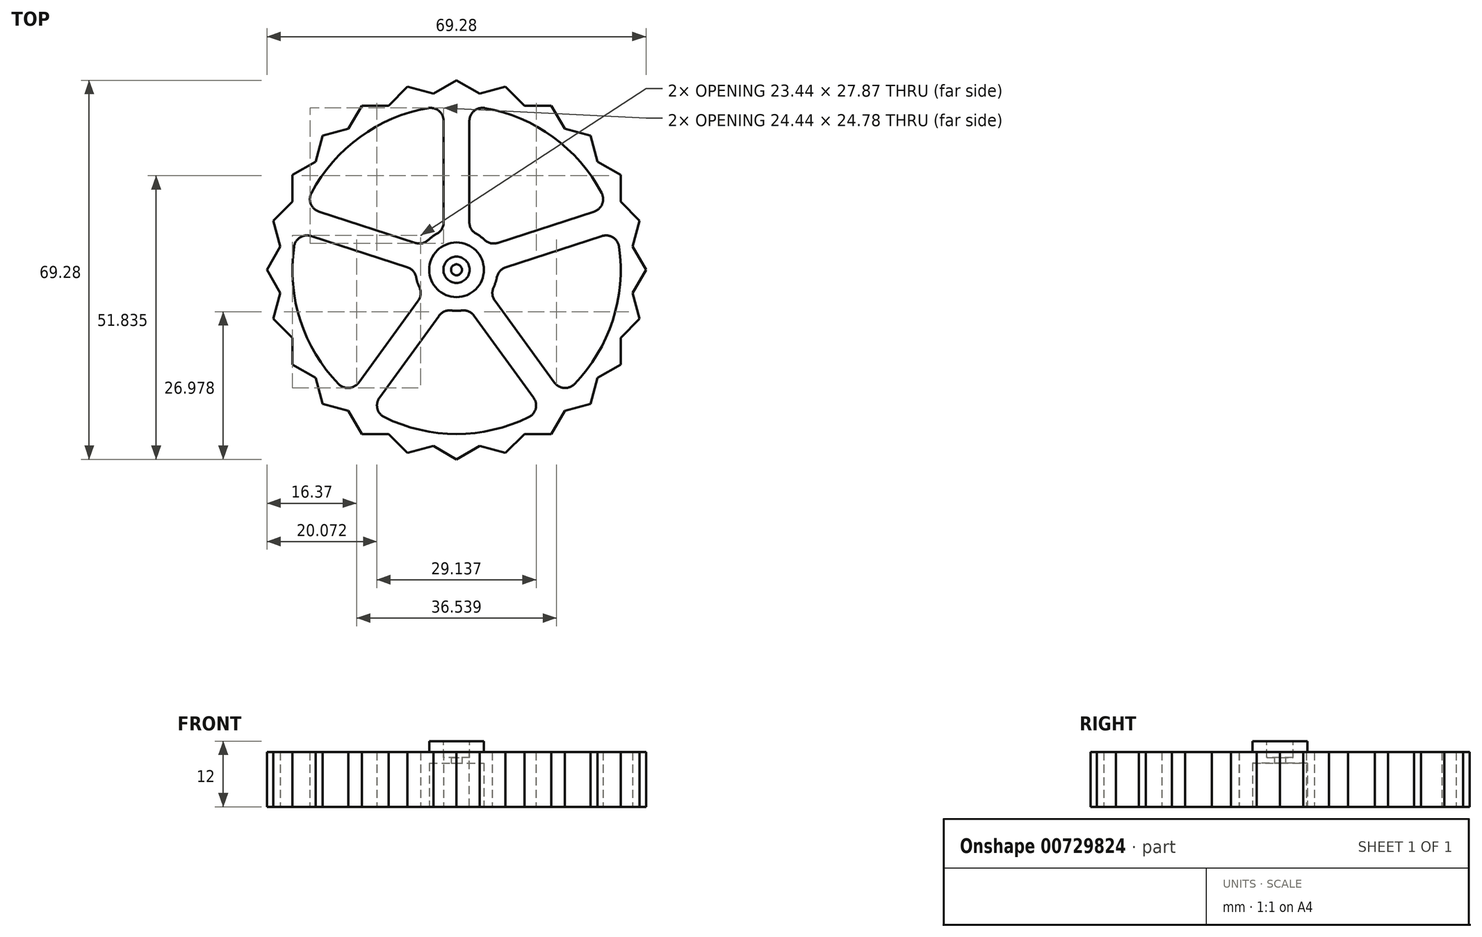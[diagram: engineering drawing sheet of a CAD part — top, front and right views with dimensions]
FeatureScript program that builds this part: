
annotation { "Feature Type Name" : "Feature", "Feature Type Description" : "" }
export const myFeature = defineFeature(function(context is Context, id is Id, definition is map)
    precondition{}
    {
        {
            var Q0;
            Q0=qCreatedBy(makeId("Top.planeOp"),FACE);
            var sketch = newSketch(context, id + "F0", { "sketchPlane" : qUnion([Q0])});
            skCircle(sketch, "E0", {"center": v(0, 0) * mm, "radius": 30 * mm});
            skCircle(sketch, "E1", {"center": v(0, 0) * mm, "radius": 2.35 * mm});
            skCircle(sketch, "E2.cCircle", {"center": v(0, 0) * mm, "radius": 30 * mm, "construction": true});
            skLineSegment(sketch, "E2.0", {"start": v(-17.32, 30) * mm, "end": v(17.32, 30) * mm});
            skLineSegment(sketch, "E2.1", {"start": v(17.32, 30) * mm, "end": v(34.64, 0) * mm});
            skLineSegment(sketch, "E2.2", {"start": v(34.64, 0) * mm, "end": v(17.32, -30) * mm});
            skLineSegment(sketch, "E2.3", {"start": v(17.32, -30) * mm, "end": v(-17.32, -30) * mm});
            skLineSegment(sketch, "E2.4", {"start": v(-17.32, -30) * mm, "end": v(-34.64, 0) * mm});
            skLineSegment(sketch, "E2.5", {"start": v(-34.64, 0) * mm, "end": v(-17.32, 30) * mm});
            skPoint(sketch, "E2.0.midPoint", {"position": v(0, 30) * mm});
            skLineSegment(sketch, "E3", {"start": v(0, 0) * mm, "end": v(25.98, 15) * mm, "construction": true});
            skLineSegment(sketch, "E4.0", {"start": v(30, 17.32) * mm, "end": v(30, -17.32) * mm});
            skLineSegment(sketch, "E4.1", {"start": v(30, -17.32) * mm, "end": v(0, -34.64) * mm});
            skLineSegment(sketch, "E4.2", {"start": v(0, -34.64) * mm, "end": v(-30, -17.32) * mm});
            skLineSegment(sketch, "E4.3", {"start": v(-30, -17.32) * mm, "end": v(-30, 17.32) * mm});
            skLineSegment(sketch, "E4.4", {"start": v(-30, 17.32) * mm, "end": v(0, 34.64) * mm});
            skLineSegment(sketch, "E4.5", {"start": v(0, 34.64) * mm, "end": v(30, 17.32) * mm});
            skPoint(sketch, "E4.0.midPoint", {"position": v(30, 0) * mm});
            skLineSegment(sketch, "E5", {"start": v(0, 0) * mm, "end": v(21.96, 21.96) * mm, "construction": true});
            skLineSegment(sketch, "E6.0", {"start": v(8.97, 33.46) * mm, "end": v(33.46, 8.97) * mm});
            skLineSegment(sketch, "E6.1", {"start": v(33.46, 8.97) * mm, "end": v(24.5, -24.5) * mm});
            skLineSegment(sketch, "E6.2", {"start": v(24.5, -24.5) * mm, "end": v(-8.97, -33.46) * mm});
            skLineSegment(sketch, "E6.3", {"start": v(-8.97, -33.46) * mm, "end": v(-33.46, -8.97) * mm});
            skLineSegment(sketch, "E6.4", {"start": v(-33.46, -8.97) * mm, "end": v(-24.5, 24.5) * mm});
            skLineSegment(sketch, "E6.5", {"start": v(-24.5, 24.5) * mm, "end": v(8.97, 33.46) * mm});
            skPoint(sketch, "E6.0.midPoint", {"position": v(21.21, 21.21) * mm});
            skLineSegment(sketch, "E7", {"start": v(0, 0) * mm, "end": v(30, 8.04) * mm, "construction": true});
            skLineSegment(sketch, "E8.0", {"start": v(24.5, 24.5) * mm, "end": v(33.46, -8.97) * mm});
            skLineSegment(sketch, "E8.1", {"start": v(33.46, -8.97) * mm, "end": v(8.97, -33.46) * mm});
            skLineSegment(sketch, "E8.2", {"start": v(8.97, -33.46) * mm, "end": v(-24.5, -24.5) * mm});
            skLineSegment(sketch, "E8.3", {"start": v(-24.5, -24.5) * mm, "end": v(-33.46, 8.97) * mm});
            skLineSegment(sketch, "E8.4", {"start": v(-33.46, 8.97) * mm, "end": v(-8.97, 33.46) * mm});
            skLineSegment(sketch, "E8.5", {"start": v(-8.97, 33.46) * mm, "end": v(24.5, 24.5) * mm});
            skPoint(sketch, "E8.0.midPoint", {"position": v(28.98, 7.76) * mm});
            skLineSegment(sketch, "E9", {"start": v(-25, 0) * mm, "end": v(22.68, 0) * mm, "construction": true});
            skLineSegment(sketch, "E10", {"start": v(-2.35, 0) * mm, "end": v(-2.35, 29.9) * mm});
            skLineSegment(sketch, "E11", {"start": v(2.35, 0) * mm, "end": v(2.35, 29.9) * mm});
            skLineSegment(sketch, "E12.1.0", {"start": v(0.73, 2.23) * mm, "end": v(-27.72, 11.48) * mm});
            skLineSegment(sketch, "E12.1.1", {"start": v(-0.73, -2.23) * mm, "end": v(-29.17, 7) * mm});
            skLineSegment(sketch, "E12.2.0", {"start": v(-1.9, 1.38) * mm, "end": v(-19.48, -22.81) * mm});
            skLineSegment(sketch, "E12.2.1", {"start": v(1.9, -1.38) * mm, "end": v(-15.68, -25.58) * mm});
            skLineSegment(sketch, "E12.3.0", {"start": v(-1.9, -1.38) * mm, "end": v(15.68, -25.58) * mm});
            skLineSegment(sketch, "E12.3.1", {"start": v(1.9, 1.38) * mm, "end": v(19.48, -22.81) * mm});
            skLineSegment(sketch, "E12.4.0", {"start": v(0.73, -2.23) * mm, "end": v(29.17, 7) * mm});
            skLineSegment(sketch, "E12.4.1", {"start": v(-0.73, 2.23) * mm, "end": v(27.72, 11.48) * mm});
            skCircle(sketch, "E13", {"center": v(0, 0) * mm, "radius": 7.5 * mm});
            skCircle(sketch, "E14", {"center": v(0, 0) * mm, "radius": 1 * mm});
            skSolve(sketch);
        }
        {
            var Q0;
            {var subQ0=sQuery(id+"F0.wireOp",EDGE,"E12.1.0");var subQ1=sQuery(id+"F0.wireOp",EDGE,"E0");var subQ2=makeQuery(id+"F0.imprint","INTERSECT",VERTEX,{"derivedFrom":[subQ1,subQ0]});Q0=makeQuery(id+"F0.imprint","IMPRINT",FACE,{"disambiguationData":[TD([[makeQuery(id+"F0.imprint","IMPRINT",EDGE,{"disambiguationData":[TD([[subQ2,-1.0]])],"derivedFrom":subQ1}),1.0]])]});}
            var Q1;
            {var subQ0=sQuery(id+"F0.wireOp",EDGE,"E12.2.0");var subQ1=sQuery(id+"F0.wireOp",EDGE,"E10");var subQ2=makeQuery(id+"F0.imprint","INTERSECT",VERTEX,{"derivedFrom":[subQ1,subQ0]});Q1=makeQuery(id+"F0.imprint","IMPRINT",FACE,{"disambiguationData":[TD([[makeQuery(id+"F0.imprint","IMPRINT",EDGE,{"disambiguationData":[TD([[subQ2,-1.0]])],"derivedFrom":subQ1}),1.0]])]});}
            var Q2;
            Q2=makeQuery(id+"F0.imprint","IMPRINT",FACE,{"disambiguationData":[TD([[makeQuery(id+"F0.imprint","IMPRINT",EDGE,{"derivedFrom":sQuery(id+"F0.wireOp",EDGE,"E14")}),-1.0]])]});
            var Q3;
            {var subQ0=sQuery(id+"F0.wireOp",EDGE,"E12.1.0");var subQ1=sQuery(id+"F0.wireOp",EDGE,"E10");var subQ2=makeQuery(id+"F0.imprint","INTERSECT",VERTEX,{"derivedFrom":[subQ1,subQ0]});Q3=makeQuery(id+"F0.imprint","IMPRINT",FACE,{"disambiguationData":[TD([[makeQuery(id+"F0.imprint","IMPRINT",EDGE,{"disambiguationData":[TD([[subQ2,-1.0]])],"derivedFrom":subQ1}),1.0]])]});}
            var Q4;
            {var subQ0=sQuery(id+"F0.wireOp",EDGE,"E12.1.0");var subQ1=sQuery(id+"F0.wireOp",EDGE,"E10");var subQ2=makeQuery(id+"F0.imprint","INTERSECT",VERTEX,{"derivedFrom":[subQ1,subQ0]});Q4=makeQuery(id+"F0.imprint","IMPRINT",FACE,{"disambiguationData":[TD([[makeQuery(id+"F0.imprint","IMPRINT",EDGE,{"disambiguationData":[TD([[subQ2,-1.0]])],"derivedFrom":subQ1}),-1.0]])]});}
            var Q5;
            {var subQ0=sQuery(id+"F0.wireOp",EDGE,"E12.4.0");var subQ1=sQuery(id+"F0.wireOp",EDGE,"E12.3.1");var subQ2=makeQuery(id+"F0.imprint","INTERSECT",VERTEX,{"derivedFrom":[subQ1,subQ0]});Q5=makeQuery(id+"F0.imprint","IMPRINT",FACE,{"disambiguationData":[TD([[makeQuery(id+"F0.imprint","IMPRINT",EDGE,{"disambiguationData":[TD([[subQ2,-1.0]])],"derivedFrom":subQ1}),1.0]])]});}
            var Q6;
            {var subQ0=sQuery(id+"F0.wireOp",EDGE,"E12.3.0");var subQ1=sQuery(id+"F0.wireOp",EDGE,"E12.1.1");var subQ2=makeQuery(id+"F0.imprint","INTERSECT",VERTEX,{"derivedFrom":[subQ1,subQ0]});Q6=makeQuery(id+"F0.imprint","IMPRINT",FACE,{"disambiguationData":[TD([[makeQuery(id+"F0.imprint","IMPRINT",EDGE,{"disambiguationData":[TD([[subQ2,-1.0]])],"derivedFrom":subQ1}),1.0]])]});}
            var Q7;
            {var subQ0=sQuery(id+"F0.wireOp",EDGE,"E12.2.0");var subQ1=sQuery(id+"F0.wireOp",EDGE,"E12.1.1");var subQ2=makeQuery(id+"F0.imprint","INTERSECT",VERTEX,{"derivedFrom":[subQ1,subQ0]});Q7=makeQuery(id+"F0.imprint","IMPRINT",FACE,{"disambiguationData":[TD([[makeQuery(id+"F0.imprint","IMPRINT",EDGE,{"disambiguationData":[TD([[subQ2,-1.0]])],"derivedFrom":subQ1}),1.0]])]});}
            var Q8;
            {var subQ1=sQuery(id+"F0.wireOp",EDGE,"E1");var subQ5=sQuery(id+"F0.wireOp",EDGE,"E12.1.0");var subQ6=makeQuery(id+"F0.imprint","INTERSECT",VERTEX,{"derivedFrom":[subQ1,subQ5]});Q8=makeQuery(id+"F0.imprint","IMPRINT",FACE,{"disambiguationData":[TD([[makeQuery(id+"F0.imprint","IMPRINT",EDGE,{"disambiguationData":[TD([[subQ6,1.0]])],"derivedFrom":subQ1}),-1.0]])]});}
            var Q9;
            {var subQ1=sQuery(id+"F0.wireOp",EDGE,"E11");var subQ5=sQuery(id+"F0.wireOp",EDGE,"E12.3.1");var subQ6=makeQuery(id+"F0.imprint","INTERSECT",VERTEX,{"derivedFrom":[subQ1,subQ5]});Q9=makeQuery(id+"F0.imprint","IMPRINT",FACE,{"disambiguationData":[TD([[makeQuery(id+"F0.imprint","IMPRINT",EDGE,{"disambiguationData":[TD([[subQ6,-1.0]])],"derivedFrom":subQ1}),-1.0]])]});}
            var Q10;
            {var subQ0=sQuery(id+"F0.wireOp",EDGE,"E12.3.0");var subQ1=sQuery(id+"F0.wireOp",EDGE,"E12.2.1");var subQ2=makeQuery(id+"F0.imprint","INTERSECT",VERTEX,{"derivedFrom":[subQ1,subQ0]});Q10=makeQuery(id+"F0.imprint","IMPRINT",FACE,{"disambiguationData":[TD([[makeQuery(id+"F0.imprint","IMPRINT",EDGE,{"disambiguationData":[TD([[subQ2,-1.0]])],"derivedFrom":subQ1}),1.0]])]});}
            var Q11;
            {var subQ5=sQuery(id+"F0.wireOp",EDGE,"E12.2.0");var subQ6=sQuery(id+"F0.wireOp",EDGE,"E1");var subQ7=makeQuery(id+"F0.imprint","INTERSECT",VERTEX,{"derivedFrom":[subQ6,subQ5]});Q11=makeQuery(id+"F0.imprint","IMPRINT",FACE,{"disambiguationData":[TD([[makeQuery(id+"F0.imprint","IMPRINT",EDGE,{"disambiguationData":[TD([[subQ7,1.0]])],"derivedFrom":subQ6}),-1.0]])]});}
            var Q12;
            {var subQ1=sQuery(id+"F0.wireOp",EDGE,"E1");var subQ6=sQuery(id+"F0.wireOp",EDGE,"E11");var subQ9=makeQuery(id+"F0.imprint","INTERSECT",VERTEX,{"derivedFrom":[subQ1,subQ6]});Q12=makeQuery(id+"F0.imprint","IMPRINT",FACE,{"disambiguationData":[TD([[makeQuery(id+"F0.imprint","IMPRINT",EDGE,{"disambiguationData":[TD([[subQ9,1.0]])],"derivedFrom":subQ1}),-1.0]])]});}
            var Q13;
            {var subQ1=sQuery(id+"F0.wireOp",EDGE,"E10");var subQ5=sQuery(id+"F0.wireOp",EDGE,"E1");var subQ6=makeQuery(id+"F0.imprint","INTERSECT",VERTEX,{"derivedFrom":[subQ5,subQ1]});Q13=makeQuery(id+"F0.imprint","IMPRINT",FACE,{"disambiguationData":[TD([[makeQuery(id+"F0.imprint","IMPRINT",EDGE,{"disambiguationData":[TD([[subQ6,-1.0]])],"derivedFrom":subQ5}),-1.0]])]});}
            var Q14;
            {var subQ0=sQuery(id+"F0.wireOp",EDGE,"E12.4.0");var subQ1=sQuery(id+"F0.wireOp",EDGE,"E12.2.1");var subQ2=makeQuery(id+"F0.imprint","INTERSECT",VERTEX,{"derivedFrom":[subQ1,subQ0]});Q14=makeQuery(id+"F0.imprint","IMPRINT",FACE,{"disambiguationData":[TD([[makeQuery(id+"F0.imprint","IMPRINT",EDGE,{"disambiguationData":[TD([[subQ2,-1.0]])],"derivedFrom":subQ1}),1.0]])]});}
            var Q15;
            {var subQ0=sQuery(id+"F0.wireOp",EDGE,"E12.4.1");var subQ1=sQuery(id+"F0.wireOp",EDGE,"E11");var subQ2=makeQuery(id+"F0.imprint","INTERSECT",VERTEX,{"derivedFrom":[subQ1,subQ0]});Q15=makeQuery(id+"F0.imprint","IMPRINT",FACE,{"disambiguationData":[TD([[makeQuery(id+"F0.imprint","IMPRINT",EDGE,{"disambiguationData":[TD([[subQ2,-1.0]])],"derivedFrom":subQ1}),-1.0]])]});}
            var Q16;
            {var subQ5=sQuery(id+"F0.wireOp",EDGE,"E1");var subQ7=sQuery(id+"F0.wireOp",EDGE,"E12.1.1");var subQ8=makeQuery(id+"F0.imprint","INTERSECT",VERTEX,{"derivedFrom":[subQ5,subQ7]});Q16=makeQuery(id+"F0.imprint","IMPRINT",FACE,{"disambiguationData":[TD([[makeQuery(id+"F0.imprint","IMPRINT",EDGE,{"disambiguationData":[TD([[subQ8,-1.0]])],"derivedFrom":subQ5}),-1.0]])]});}
            var Q17;
            {var subQ0=sQuery(id+"F0.wireOp",EDGE,"E12.1.1");var subQ1=sQuery(id+"F0.wireOp",EDGE,"E1");var subQ2=makeQuery(id+"F0.imprint","INTERSECT",VERTEX,{"derivedFrom":[subQ1,subQ0]});Q17=makeQuery(id+"F0.imprint","IMPRINT",FACE,{"disambiguationData":[TD([[makeQuery(id+"F0.imprint","IMPRINT",EDGE,{"disambiguationData":[TD([[subQ2,1.0]])],"derivedFrom":subQ1}),-1.0]])]});}
            var Q18;
            {var subQ0=sQuery(id+"F0.wireOp",EDGE,"E11");var subQ1=sQuery(id+"F0.wireOp",EDGE,"E1");var subQ2=makeQuery(id+"F0.imprint","INTERSECT",VERTEX,{"derivedFrom":[subQ1,subQ0]});Q18=makeQuery(id+"F0.imprint","IMPRINT",FACE,{"disambiguationData":[TD([[makeQuery(id+"F0.imprint","IMPRINT",EDGE,{"disambiguationData":[TD([[subQ2,-1.0]])],"derivedFrom":subQ1}),-1.0]])]});}
            var Q19;
            {var subQ0=sQuery(id+"F0.wireOp",EDGE,"E10");var subQ1=sQuery(id+"F0.wireOp",EDGE,"E1");var subQ2=makeQuery(id+"F0.imprint","INTERSECT",VERTEX,{"derivedFrom":[subQ1,subQ0]});Q19=makeQuery(id+"F0.imprint","IMPRINT",FACE,{"disambiguationData":[TD([[makeQuery(id+"F0.imprint","IMPRINT",EDGE,{"disambiguationData":[TD([[subQ2,1.0]])],"derivedFrom":subQ1}),-1.0]])]});}
            var Q20;
            {var subQ0=sQuery(id+"F0.wireOp",EDGE,"E12.2.1");var subQ1=sQuery(id+"F0.wireOp",EDGE,"E1");var subQ2=makeQuery(id+"F0.imprint","INTERSECT",VERTEX,{"derivedFrom":[subQ1,subQ0]});Q20=makeQuery(id+"F0.imprint","IMPRINT",FACE,{"disambiguationData":[TD([[makeQuery(id+"F0.imprint","IMPRINT",EDGE,{"disambiguationData":[TD([[subQ2,1.0]])],"derivedFrom":subQ1}),-1.0]])]});}
            var Q21;
            {var subQ0=sQuery(id+"F0.wireOp",EDGE,"E12.1.0");var subQ1=sQuery(id+"F0.wireOp",EDGE,"E1");var subQ2=makeQuery(id+"F0.imprint","INTERSECT",VERTEX,{"derivedFrom":[subQ1,subQ0]});Q21=makeQuery(id+"F0.imprint","IMPRINT",FACE,{"disambiguationData":[TD([[makeQuery(id+"F0.imprint","IMPRINT",EDGE,{"disambiguationData":[TD([[subQ2,-1.0]])],"derivedFrom":subQ1}),-1.0]])]});}
            var Q22;
            {var subQ0=sQuery(id+"F0.wireOp",EDGE,"E12.3.0");var subQ1=sQuery(id+"F0.wireOp",EDGE,"E0");var subQ2=makeQuery(id+"F0.imprint","INTERSECT",VERTEX,{"derivedFrom":[subQ1,subQ0]});Q22=makeQuery(id+"F0.imprint","IMPRINT",FACE,{"disambiguationData":[TD([[makeQuery(id+"F0.imprint","IMPRINT",EDGE,{"disambiguationData":[TD([[subQ2,-1.0]])],"derivedFrom":subQ1}),1.0]])]});}
            var Q23;
            {var subQ0=sQuery(id+"F0.wireOp",EDGE,"E12.2.0");var subQ1=sQuery(id+"F0.wireOp",EDGE,"E0");var subQ2=makeQuery(id+"F0.imprint","INTERSECT",VERTEX,{"derivedFrom":[subQ1,subQ0]});Q23=makeQuery(id+"F0.imprint","IMPRINT",FACE,{"disambiguationData":[TD([[makeQuery(id+"F0.imprint","IMPRINT",EDGE,{"disambiguationData":[TD([[subQ2,-1.0]])],"derivedFrom":subQ1}),1.0]])]});}
            var Q24;
            {var subQ1=sQuery(id+"F0.wireOp",EDGE,"E0");var subQ5=sQuery(id+"F0.wireOp",EDGE,"E11");var subQ6=makeQuery(id+"F0.imprint","INTERSECT",VERTEX,{"derivedFrom":[subQ1,subQ5]});Q24=makeQuery(id+"F0.imprint","IMPRINT",FACE,{"disambiguationData":[TD([[makeQuery(id+"F0.imprint","IMPRINT",EDGE,{"disambiguationData":[TD([[subQ6,-1.0]])],"derivedFrom":subQ1}),1.0]])]});}
            var Q25;
            {var subQ1=sQuery(id+"F0.wireOp",EDGE,"E0");var subQ6=sQuery(id+"F0.wireOp",EDGE,"E12.4.0");var subQ7=makeQuery(id+"F0.imprint","INTERSECT",VERTEX,{"derivedFrom":[subQ1,subQ6]});Q25=makeQuery(id+"F0.imprint","IMPRINT",FACE,{"disambiguationData":[TD([[makeQuery(id+"F0.imprint","IMPRINT",EDGE,{"disambiguationData":[TD([[subQ7,-1.0]])],"derivedFrom":subQ1}),1.0]])]});}
            var Q26;
            {var subQ0=sQuery(id+"F0.wireOp",EDGE,"E6.5");var subQ1=sQuery(id+"F0.wireOp",EDGE,"E0");var subQ2=makeQuery(id+"F0.imprint","INTERSECT",VERTEX,{"derivedFrom":[subQ1,subQ0]});Q26=makeQuery(id+"F0.imprint","IMPRINT",FACE,{"disambiguationData":[TD([[makeQuery(id+"F0.imprint","IMPRINT",EDGE,{"disambiguationData":[TD([[subQ2,-1.0]])],"derivedFrom":subQ1}),-1.0]])]});}
            var Q27;
            {var subQ0=sQuery(id+"F0.wireOp",EDGE,"E2.5");var subQ1=sQuery(id+"F0.wireOp",EDGE,"E2.0");var subQ2=makeQuery(id+"F0.imprint","INTERSECT",VERTEX,{"derivedFrom":[subQ1,subQ0]});Q27=makeQuery(id+"F0.imprint","IMPRINT",FACE,{"disambiguationData":[TD([[makeQuery(id+"F0.imprint","IMPRINT",EDGE,{"disambiguationData":[TD([[subQ2,-1.0]])],"derivedFrom":subQ1}),-1.0]])]});}
            var Q28;
            {var subQ0=sQuery(id+"F0.wireOp",EDGE,"E8.4");var subQ1=sQuery(id+"F0.wireOp",EDGE,"E2.0");var subQ2=makeQuery(id+"F0.imprint","INTERSECT",VERTEX,{"derivedFrom":[subQ1,subQ0]});Q28=makeQuery(id+"F0.imprint","IMPRINT",FACE,{"disambiguationData":[TD([[makeQuery(id+"F0.imprint","IMPRINT",EDGE,{"disambiguationData":[TD([[subQ2,-1.0]])],"derivedFrom":subQ1}),-1.0]])]});}
            var Q29;
            {var subQ0=sQuery(id+"F0.wireOp",EDGE,"E4.4");var subQ1=makeQuery(id+"F0.imprint","INTERSECT",VERTEX,{"derivedFrom":[sQuery(id+"F0.wireOp",EDGE,"E0"),subQ0]});Q29=makeQuery(id+"F0.imprint","IMPRINT",FACE,{"disambiguationData":[TD([[makeQuery(id+"F0.imprint","IMPRINT",EDGE,{"disambiguationData":[TD([[subQ1,1.0]])],"derivedFrom":subQ0}),1.0]])]});}
            var Q30;
            {var subQ0=sQuery(id+"F0.wireOp",EDGE,"E8.4");var subQ1=sQuery(id+"F0.wireOp",EDGE,"E0");var subQ2=makeQuery(id+"F0.imprint","INTERSECT",VERTEX,{"derivedFrom":[subQ1,subQ0]});Q30=makeQuery(id+"F0.imprint","IMPRINT",FACE,{"disambiguationData":[TD([[makeQuery(id+"F0.imprint","IMPRINT",EDGE,{"disambiguationData":[TD([[subQ2,-1.0]])],"derivedFrom":subQ1}),-1.0]])]});}
            var Q31;
            {var subQ0=sQuery(id+"F0.wireOp",EDGE,"E8.4");var subQ1=sQuery(id+"F0.wireOp",EDGE,"E2.5");var subQ2=makeQuery(id+"F0.imprint","INTERSECT",VERTEX,{"derivedFrom":[subQ1,subQ0]});Q31=makeQuery(id+"F0.imprint","IMPRINT",FACE,{"disambiguationData":[TD([[makeQuery(id+"F0.imprint","IMPRINT",EDGE,{"disambiguationData":[TD([[subQ2,-1.0]])],"derivedFrom":subQ1}),1.0]])]});}
            var Q32;
            {var subQ0=sQuery(id+"F0.wireOp",EDGE,"E6.5");var subQ1=sQuery(id+"F0.wireOp",EDGE,"E2.5");var subQ2=makeQuery(id+"F0.imprint","INTERSECT",VERTEX,{"derivedFrom":[subQ1,subQ0]});Q32=makeQuery(id+"F0.imprint","IMPRINT",FACE,{"disambiguationData":[TD([[makeQuery(id+"F0.imprint","IMPRINT",EDGE,{"disambiguationData":[TD([[subQ2,1.0]])],"derivedFrom":subQ1}),1.0]])]});}
            var Q33;
            {var subQ0=sQuery(id+"F0.wireOp",EDGE,"E6.5");var subQ1=sQuery(id+"F0.wireOp",EDGE,"E2.5");var subQ2=makeQuery(id+"F0.imprint","INTERSECT",VERTEX,{"derivedFrom":[subQ1,subQ0]});Q33=makeQuery(id+"F0.imprint","IMPRINT",FACE,{"disambiguationData":[TD([[makeQuery(id+"F0.imprint","IMPRINT",EDGE,{"disambiguationData":[TD([[subQ2,1.0]])],"derivedFrom":subQ1}),-1.0]])]});}
            var Q34;
            {var subQ0=sQuery(id+"F0.wireOp",EDGE,"E4.3");var subQ1=sQuery(id+"F0.wireOp",EDGE,"E2.5");var subQ2=makeQuery(id+"F0.imprint","INTERSECT",VERTEX,{"derivedFrom":[subQ1,subQ0]});Q34=makeQuery(id+"F0.imprint","IMPRINT",FACE,{"disambiguationData":[TD([[makeQuery(id+"F0.imprint","IMPRINT",EDGE,{"disambiguationData":[TD([[subQ2,-1.0]])],"derivedFrom":subQ1}),1.0]])]});}
            var Q35;
            {var subQ0=sQuery(id+"F0.wireOp",EDGE,"E0");var subQ1=makeQuery(id+"F0.imprint","INTERSECT",VERTEX,{"derivedFrom":[subQ0,sQuery(id+"F0.wireOp",EDGE,"E12.1.0")]});Q35=makeQuery(id+"F0.imprint","IMPRINT",FACE,{"disambiguationData":[TD([[makeQuery(id+"F0.imprint","IMPRINT",EDGE,{"disambiguationData":[TD([[subQ1,1.0]])],"derivedFrom":subQ0}),-1.0]])]});}
            var Q36;
            {var subQ0=sQuery(id+"F0.wireOp",EDGE,"E4.4");var subQ1=sQuery(id+"F0.wireOp",EDGE,"E4.3");var subQ2=makeQuery(id+"F0.imprint","INTERSECT",VERTEX,{"derivedFrom":[subQ1,subQ0]});Q36=makeQuery(id+"F0.imprint","IMPRINT",FACE,{"disambiguationData":[TD([[makeQuery(id+"F0.imprint","IMPRINT",EDGE,{"disambiguationData":[TD([[subQ2,1.0]])],"derivedFrom":subQ1}),-1.0]])]});}
            var Q37;
            {var subQ0=sQuery(id+"F0.wireOp",EDGE,"E2.5");var subQ1=makeQuery(id+"F0.imprint","INTERSECT",VERTEX,{"derivedFrom":[sQuery(id+"F0.wireOp",EDGE,"E0"),subQ0]});Q37=makeQuery(id+"F0.imprint","IMPRINT",FACE,{"disambiguationData":[TD([[makeQuery(id+"F0.imprint","IMPRINT",EDGE,{"disambiguationData":[TD([[subQ1,1.0]])],"derivedFrom":subQ0}),1.0]])]});}
            var Q38;
            {var subQ0=sQuery(id+"F0.wireOp",EDGE,"E4.4");var subQ1=sQuery(id+"F0.wireOp",EDGE,"E0");var subQ2=makeQuery(id+"F0.imprint","INTERSECT",VERTEX,{"derivedFrom":[subQ1,subQ0]});Q38=makeQuery(id+"F0.imprint","IMPRINT",FACE,{"disambiguationData":[TD([[makeQuery(id+"F0.imprint","IMPRINT",EDGE,{"disambiguationData":[TD([[subQ2,-1.0]])],"derivedFrom":subQ1}),-1.0]])]});}
            var Q39;
            {var subQ0=sQuery(id+"F0.wireOp",EDGE,"E8.4");var subQ1=sQuery(id+"F0.wireOp",EDGE,"E2.5");var subQ2=makeQuery(id+"F0.imprint","INTERSECT",VERTEX,{"derivedFrom":[subQ1,subQ0]});Q39=makeQuery(id+"F0.imprint","IMPRINT",FACE,{"disambiguationData":[TD([[makeQuery(id+"F0.imprint","IMPRINT",EDGE,{"disambiguationData":[TD([[subQ2,-1.0]])],"derivedFrom":subQ1}),-1.0]])]});}
            var Q40;
            {var subQ0=sQuery(id+"F0.wireOp",EDGE,"E8.3");var subQ1=sQuery(id+"F0.wireOp",EDGE,"E2.5");var subQ2=makeQuery(id+"F0.imprint","INTERSECT",VERTEX,{"derivedFrom":[subQ1,subQ0]});Q40=makeQuery(id+"F0.imprint","IMPRINT",FACE,{"disambiguationData":[TD([[makeQuery(id+"F0.imprint","IMPRINT",EDGE,{"disambiguationData":[TD([[subQ2,-1.0]])],"derivedFrom":subQ1}),-1.0]])]});}
            var Q41;
            {var subQ0=sQuery(id+"F0.wireOp",EDGE,"E4.3");var subQ1=sQuery(id+"F0.wireOp",EDGE,"E4.2");var subQ2=makeQuery(id+"F0.imprint","INTERSECT",VERTEX,{"derivedFrom":[subQ1,subQ0]});Q41=makeQuery(id+"F0.imprint","IMPRINT",FACE,{"disambiguationData":[TD([[makeQuery(id+"F0.imprint","IMPRINT",EDGE,{"disambiguationData":[TD([[subQ2,1.0]])],"derivedFrom":subQ1}),-1.0]])]});}
            var Q42;
            {var subQ0=sQuery(id+"F0.wireOp",EDGE,"E8.3");var subQ1=sQuery(id+"F0.wireOp",EDGE,"E2.4");var subQ2=makeQuery(id+"F0.imprint","INTERSECT",VERTEX,{"derivedFrom":[subQ1,subQ0]});Q42=makeQuery(id+"F0.imprint","IMPRINT",FACE,{"disambiguationData":[TD([[makeQuery(id+"F0.imprint","IMPRINT",EDGE,{"disambiguationData":[TD([[subQ2,-1.0]])],"derivedFrom":subQ1}),1.0]])]});}
            var Q43;
            {var subQ0=sQuery(id+"F0.wireOp",EDGE,"E6.4");var subQ1=sQuery(id+"F0.wireOp",EDGE,"E2.4");var subQ2=makeQuery(id+"F0.imprint","INTERSECT",VERTEX,{"derivedFrom":[subQ1,subQ0]});Q43=makeQuery(id+"F0.imprint","IMPRINT",FACE,{"disambiguationData":[TD([[makeQuery(id+"F0.imprint","IMPRINT",EDGE,{"disambiguationData":[TD([[subQ2,1.0]])],"derivedFrom":subQ1}),1.0]])]});}
            var Q44;
            {var subQ0=sQuery(id+"F0.wireOp",EDGE,"E4.3");var subQ1=makeQuery(id+"F0.imprint","INTERSECT",VERTEX,{"derivedFrom":[sQuery(id+"F0.wireOp",EDGE,"E0"),subQ0]});Q44=makeQuery(id+"F0.imprint","IMPRINT",FACE,{"disambiguationData":[TD([[makeQuery(id+"F0.imprint","IMPRINT",EDGE,{"disambiguationData":[TD([[subQ1,1.0]])],"derivedFrom":subQ0}),1.0]])]});}
            var Q45;
            {var subQ0=sQuery(id+"F0.wireOp",EDGE,"E8.3");var subQ1=sQuery(id+"F0.wireOp",EDGE,"E2.4");var subQ2=makeQuery(id+"F0.imprint","INTERSECT",VERTEX,{"derivedFrom":[subQ1,subQ0]});Q45=makeQuery(id+"F0.imprint","IMPRINT",FACE,{"disambiguationData":[TD([[makeQuery(id+"F0.imprint","IMPRINT",EDGE,{"disambiguationData":[TD([[subQ2,-1.0]])],"derivedFrom":subQ1}),-1.0]])]});}
            var Q46;
            {var subQ0=sQuery(id+"F0.wireOp",EDGE,"E2.5");var subQ1=sQuery(id+"F0.wireOp",EDGE,"E2.4");var subQ2=makeQuery(id+"F0.imprint","INTERSECT",VERTEX,{"derivedFrom":[subQ1,subQ0]});Q46=makeQuery(id+"F0.imprint","IMPRINT",FACE,{"disambiguationData":[TD([[makeQuery(id+"F0.imprint","IMPRINT",EDGE,{"disambiguationData":[TD([[subQ2,1.0]])],"derivedFrom":subQ1}),-1.0]])]});}
            var Q47;
            {var subQ0=sQuery(id+"F0.wireOp",EDGE,"E8.3");var subQ1=sQuery(id+"F0.wireOp",EDGE,"E0");var subQ2=makeQuery(id+"F0.imprint","INTERSECT",VERTEX,{"derivedFrom":[subQ1,subQ0]});Q47=makeQuery(id+"F0.imprint","IMPRINT",FACE,{"disambiguationData":[TD([[makeQuery(id+"F0.imprint","IMPRINT",EDGE,{"disambiguationData":[TD([[subQ2,-1.0]])],"derivedFrom":subQ1}),-1.0]])]});}
            var Q48;
            {var subQ0=sQuery(id+"F0.wireOp",EDGE,"E6.4");var subQ1=sQuery(id+"F0.wireOp",EDGE,"E2.4");var subQ2=makeQuery(id+"F0.imprint","INTERSECT",VERTEX,{"derivedFrom":[subQ1,subQ0]});Q48=makeQuery(id+"F0.imprint","IMPRINT",FACE,{"disambiguationData":[TD([[makeQuery(id+"F0.imprint","IMPRINT",EDGE,{"disambiguationData":[TD([[subQ2,1.0]])],"derivedFrom":subQ1}),-1.0]])]});}
            var Q49;
            {var subQ0=sQuery(id+"F0.wireOp",EDGE,"E4.3");var subQ1=sQuery(id+"F0.wireOp",EDGE,"E0");var subQ2=makeQuery(id+"F0.imprint","INTERSECT",VERTEX,{"derivedFrom":[subQ1,subQ0]});Q49=makeQuery(id+"F0.imprint","IMPRINT",FACE,{"disambiguationData":[TD([[makeQuery(id+"F0.imprint","IMPRINT",EDGE,{"disambiguationData":[TD([[subQ2,-1.0]])],"derivedFrom":subQ1}),-1.0]])]});}
            var Q50;
            {var subQ0=sQuery(id+"F0.wireOp",EDGE,"E8.3");var subQ1=sQuery(id+"F0.wireOp",EDGE,"E2.5");var subQ2=makeQuery(id+"F0.imprint","INTERSECT",VERTEX,{"derivedFrom":[subQ1,subQ0]});Q50=makeQuery(id+"F0.imprint","IMPRINT",FACE,{"disambiguationData":[TD([[makeQuery(id+"F0.imprint","IMPRINT",EDGE,{"disambiguationData":[TD([[subQ2,-1.0]])],"derivedFrom":subQ1}),1.0]])]});}
            var Q51;
            {var subQ0=sQuery(id+"F0.wireOp",EDGE,"E0");var subQ1=makeQuery(id+"F0.imprint","INTERSECT",VERTEX,{"derivedFrom":[subQ0,sQuery(id+"F0.wireOp",EDGE,"E12.1.1")]});Q51=makeQuery(id+"F0.imprint","IMPRINT",FACE,{"disambiguationData":[TD([[makeQuery(id+"F0.imprint","IMPRINT",EDGE,{"disambiguationData":[TD([[subQ1,1.0]])],"derivedFrom":subQ0}),-1.0]])]});}
            var Q52;
            {var subQ0=sQuery(id+"F0.wireOp",EDGE,"E4.3");var subQ1=sQuery(id+"F0.wireOp",EDGE,"E2.5");var subQ2=makeQuery(id+"F0.imprint","INTERSECT",VERTEX,{"derivedFrom":[subQ1,subQ0]});Q52=makeQuery(id+"F0.imprint","IMPRINT",FACE,{"disambiguationData":[TD([[makeQuery(id+"F0.imprint","IMPRINT",EDGE,{"disambiguationData":[TD([[subQ2,-1.0]])],"derivedFrom":subQ1}),-1.0]])]});}
            var Q53;
            {var subQ0=sQuery(id+"F0.wireOp",EDGE,"E6.3");var subQ1=sQuery(id+"F0.wireOp",EDGE,"E2.3");var subQ2=makeQuery(id+"F0.imprint","INTERSECT",VERTEX,{"derivedFrom":[subQ1,subQ0]});Q53=makeQuery(id+"F0.imprint","IMPRINT",FACE,{"disambiguationData":[TD([[makeQuery(id+"F0.imprint","IMPRINT",EDGE,{"disambiguationData":[TD([[subQ2,1.0]])],"derivedFrom":subQ1}),-1.0]])]});}
            var Q54;
            {var subQ0=sQuery(id+"F0.wireOp",EDGE,"E0");var subQ7=makeQuery(id+"F0.imprint","INTERSECT",VERTEX,{"derivedFrom":[subQ0,sQuery(id+"F0.wireOp",EDGE,"E12.2.0")]});Q54=makeQuery(id+"F0.imprint","IMPRINT",FACE,{"disambiguationData":[TD([[makeQuery(id+"F0.imprint","IMPRINT",EDGE,{"disambiguationData":[TD([[subQ7,1.0]])],"derivedFrom":subQ0}),-1.0]])]});}
            var Q55;
            {var subQ0=sQuery(id+"F0.wireOp",EDGE,"E4.2");var subQ1=sQuery(id+"F0.wireOp",EDGE,"E2.4");var subQ2=makeQuery(id+"F0.imprint","INTERSECT",VERTEX,{"derivedFrom":[subQ1,subQ0]});Q55=makeQuery(id+"F0.imprint","IMPRINT",FACE,{"disambiguationData":[TD([[makeQuery(id+"F0.imprint","IMPRINT",EDGE,{"disambiguationData":[TD([[subQ2,-1.0]])],"derivedFrom":subQ1}),-1.0]])]});}
            var Q56;
            {var subQ0=sQuery(id+"F0.wireOp",EDGE,"E8.2");var subQ1=sQuery(id+"F0.wireOp",EDGE,"E2.3");var subQ2=makeQuery(id+"F0.imprint","INTERSECT",VERTEX,{"derivedFrom":[subQ1,subQ0]});Q56=makeQuery(id+"F0.imprint","IMPRINT",FACE,{"disambiguationData":[TD([[makeQuery(id+"F0.imprint","IMPRINT",EDGE,{"disambiguationData":[TD([[subQ2,-1.0]])],"derivedFrom":subQ1}),-1.0]])]});}
            var Q57;
            {var subQ0=sQuery(id+"F0.wireOp",EDGE,"E2.4");var subQ1=sQuery(id+"F0.wireOp",EDGE,"E2.3");var subQ2=makeQuery(id+"F0.imprint","INTERSECT",VERTEX,{"derivedFrom":[subQ1,subQ0]});Q57=makeQuery(id+"F0.imprint","IMPRINT",FACE,{"disambiguationData":[TD([[makeQuery(id+"F0.imprint","IMPRINT",EDGE,{"disambiguationData":[TD([[subQ2,1.0]])],"derivedFrom":subQ1}),-1.0]])]});}
            var Q58;
            {var subQ0=sQuery(id+"F0.wireOp",EDGE,"E8.2");var subQ1=sQuery(id+"F0.wireOp",EDGE,"E2.4");var subQ2=makeQuery(id+"F0.imprint","INTERSECT",VERTEX,{"derivedFrom":[subQ1,subQ0]});Q58=makeQuery(id+"F0.imprint","IMPRINT",FACE,{"disambiguationData":[TD([[makeQuery(id+"F0.imprint","IMPRINT",EDGE,{"disambiguationData":[TD([[subQ2,-1.0]])],"derivedFrom":subQ1}),1.0]])]});}
            var Q59;
            {var subQ0=sQuery(id+"F0.wireOp",EDGE,"E6.3");var subQ1=sQuery(id+"F0.wireOp",EDGE,"E2.3");var subQ2=makeQuery(id+"F0.imprint","INTERSECT",VERTEX,{"derivedFrom":[subQ1,subQ0]});Q59=makeQuery(id+"F0.imprint","IMPRINT",FACE,{"disambiguationData":[TD([[makeQuery(id+"F0.imprint","IMPRINT",EDGE,{"disambiguationData":[TD([[subQ2,1.0]])],"derivedFrom":subQ1}),1.0]])]});}
            var Q60;
            {var subQ0=sQuery(id+"F0.wireOp",EDGE,"E8.2");var subQ1=sQuery(id+"F0.wireOp",EDGE,"E2.4");var subQ2=makeQuery(id+"F0.imprint","INTERSECT",VERTEX,{"derivedFrom":[subQ1,subQ0]});Q60=makeQuery(id+"F0.imprint","IMPRINT",FACE,{"disambiguationData":[TD([[makeQuery(id+"F0.imprint","IMPRINT",EDGE,{"disambiguationData":[TD([[subQ2,-1.0]])],"derivedFrom":subQ1}),-1.0]])]});}
            var Q61;
            {var subQ0=sQuery(id+"F0.wireOp",EDGE,"E4.2");var subQ1=makeQuery(id+"F0.imprint","INTERSECT",VERTEX,{"derivedFrom":[sQuery(id+"F0.wireOp",EDGE,"E0"),subQ0]});Q61=makeQuery(id+"F0.imprint","IMPRINT",FACE,{"disambiguationData":[TD([[makeQuery(id+"F0.imprint","IMPRINT",EDGE,{"disambiguationData":[TD([[subQ1,1.0]])],"derivedFrom":subQ0}),1.0]])]});}
            var Q62;
            {var subQ0=sQuery(id+"F0.wireOp",EDGE,"E2.4");var subQ1=sQuery(id+"F0.wireOp",EDGE,"E0");var subQ2=makeQuery(id+"F0.imprint","INTERSECT",VERTEX,{"derivedFrom":[subQ1,subQ0]});Q62=makeQuery(id+"F0.imprint","IMPRINT",FACE,{"disambiguationData":[TD([[makeQuery(id+"F0.imprint","IMPRINT",EDGE,{"disambiguationData":[TD([[subQ2,-1.0]])],"derivedFrom":subQ1}),-1.0]])]});}
            var Q63;
            {var subQ0=sQuery(id+"F0.wireOp",EDGE,"E2.4");var subQ1=makeQuery(id+"F0.imprint","INTERSECT",VERTEX,{"derivedFrom":[sQuery(id+"F0.wireOp",EDGE,"E0"),subQ0]});Q63=makeQuery(id+"F0.imprint","IMPRINT",FACE,{"disambiguationData":[TD([[makeQuery(id+"F0.imprint","IMPRINT",EDGE,{"disambiguationData":[TD([[subQ1,1.0]])],"derivedFrom":subQ0}),1.0]])]});}
            var Q64;
            {var subQ0=sQuery(id+"F0.wireOp",EDGE,"E4.2");var subQ1=sQuery(id+"F0.wireOp",EDGE,"E0");var subQ2=makeQuery(id+"F0.imprint","INTERSECT",VERTEX,{"derivedFrom":[subQ1,subQ0]});Q64=makeQuery(id+"F0.imprint","IMPRINT",FACE,{"disambiguationData":[TD([[makeQuery(id+"F0.imprint","IMPRINT",EDGE,{"disambiguationData":[TD([[subQ2,-1.0]])],"derivedFrom":subQ1}),-1.0]])]});}
            var Q65;
            {var subQ0=sQuery(id+"F0.wireOp",EDGE,"E8.2");var subQ1=sQuery(id+"F0.wireOp",EDGE,"E2.3");var subQ2=makeQuery(id+"F0.imprint","INTERSECT",VERTEX,{"derivedFrom":[subQ1,subQ0]});Q65=makeQuery(id+"F0.imprint","IMPRINT",FACE,{"disambiguationData":[TD([[makeQuery(id+"F0.imprint","IMPRINT",EDGE,{"disambiguationData":[TD([[subQ2,-1.0]])],"derivedFrom":subQ1}),1.0]])]});}
            var Q66;
            {var subQ0=sQuery(id+"F0.wireOp",EDGE,"E4.2");var subQ1=sQuery(id+"F0.wireOp",EDGE,"E2.4");var subQ2=makeQuery(id+"F0.imprint","INTERSECT",VERTEX,{"derivedFrom":[subQ1,subQ0]});Q66=makeQuery(id+"F0.imprint","IMPRINT",FACE,{"disambiguationData":[TD([[makeQuery(id+"F0.imprint","IMPRINT",EDGE,{"disambiguationData":[TD([[subQ2,-1.0]])],"derivedFrom":subQ1}),1.0]])]});}
            var Q67;
            {var subQ0=sQuery(id+"F0.wireOp",EDGE,"E8.2");var subQ1=sQuery(id+"F0.wireOp",EDGE,"E0");var subQ2=makeQuery(id+"F0.imprint","INTERSECT",VERTEX,{"derivedFrom":[subQ1,subQ0]});Q67=makeQuery(id+"F0.imprint","IMPRINT",FACE,{"disambiguationData":[TD([[makeQuery(id+"F0.imprint","IMPRINT",EDGE,{"disambiguationData":[TD([[subQ2,-1.0]])],"derivedFrom":subQ1}),-1.0]])]});}
            var Q68;
            {var subQ0=sQuery(id+"F0.wireOp",EDGE,"E4.2");var subQ1=sQuery(id+"F0.wireOp",EDGE,"E4.1");var subQ2=makeQuery(id+"F0.imprint","INTERSECT",VERTEX,{"derivedFrom":[subQ1,subQ0]});Q68=makeQuery(id+"F0.imprint","IMPRINT",FACE,{"disambiguationData":[TD([[makeQuery(id+"F0.imprint","IMPRINT",EDGE,{"disambiguationData":[TD([[subQ2,1.0]])],"derivedFrom":subQ1}),-1.0]])]});}
            var Q69;
            {var subQ0=sQuery(id+"F0.wireOp",EDGE,"E8.1");var subQ1=sQuery(id+"F0.wireOp",EDGE,"E2.3");var subQ2=makeQuery(id+"F0.imprint","INTERSECT",VERTEX,{"derivedFrom":[subQ1,subQ0]});Q69=makeQuery(id+"F0.imprint","IMPRINT",FACE,{"disambiguationData":[TD([[makeQuery(id+"F0.imprint","IMPRINT",EDGE,{"disambiguationData":[TD([[subQ2,-1.0]])],"derivedFrom":subQ1}),-1.0]])]});}
            var Q70;
            {var subQ0=sQuery(id+"F0.wireOp",EDGE,"E4.1");var subQ1=sQuery(id+"F0.wireOp",EDGE,"E4.0");var subQ2=makeQuery(id+"F0.imprint","INTERSECT",VERTEX,{"derivedFrom":[subQ1,subQ0]});Q70=makeQuery(id+"F0.imprint","IMPRINT",FACE,{"disambiguationData":[TD([[makeQuery(id+"F0.imprint","IMPRINT",EDGE,{"disambiguationData":[TD([[subQ2,1.0]])],"derivedFrom":subQ1}),-1.0]])]});}
            var Q71;
            {var subQ0=sQuery(id+"F0.wireOp",EDGE,"E6.2");var subQ1=sQuery(id+"F0.wireOp",EDGE,"E2.2");var subQ2=makeQuery(id+"F0.imprint","INTERSECT",VERTEX,{"derivedFrom":[subQ1,subQ0]});Q71=makeQuery(id+"F0.imprint","IMPRINT",FACE,{"disambiguationData":[TD([[makeQuery(id+"F0.imprint","IMPRINT",EDGE,{"disambiguationData":[TD([[subQ2,1.0]])],"derivedFrom":subQ1}),1.0]])]});}
            var Q72;
            {var subQ0=sQuery(id+"F0.wireOp",EDGE,"E2.3");var subQ1=sQuery(id+"F0.wireOp",EDGE,"E2.2");var subQ2=makeQuery(id+"F0.imprint","INTERSECT",VERTEX,{"derivedFrom":[subQ1,subQ0]});Q72=makeQuery(id+"F0.imprint","IMPRINT",FACE,{"disambiguationData":[TD([[makeQuery(id+"F0.imprint","IMPRINT",EDGE,{"disambiguationData":[TD([[subQ2,1.0]])],"derivedFrom":subQ1}),-1.0]])]});}
            var Q73;
            {var subQ0=sQuery(id+"F0.wireOp",EDGE,"E8.1");var subQ1=sQuery(id+"F0.wireOp",EDGE,"E2.3");var subQ2=makeQuery(id+"F0.imprint","INTERSECT",VERTEX,{"derivedFrom":[subQ1,subQ0]});Q73=makeQuery(id+"F0.imprint","IMPRINT",FACE,{"disambiguationData":[TD([[makeQuery(id+"F0.imprint","IMPRINT",EDGE,{"disambiguationData":[TD([[subQ2,-1.0]])],"derivedFrom":subQ1}),1.0]])]});}
            var Q74;
            {var subQ0=sQuery(id+"F0.wireOp",EDGE,"E4.1");var subQ1=sQuery(id+"F0.wireOp",EDGE,"E2.3");var subQ2=makeQuery(id+"F0.imprint","INTERSECT",VERTEX,{"derivedFrom":[subQ1,subQ0]});Q74=makeQuery(id+"F0.imprint","IMPRINT",FACE,{"disambiguationData":[TD([[makeQuery(id+"F0.imprint","IMPRINT",EDGE,{"disambiguationData":[TD([[subQ2,-1.0]])],"derivedFrom":subQ1}),1.0]])]});}
            var Q75;
            {var subQ0=sQuery(id+"F0.wireOp",EDGE,"E6.2");var subQ1=sQuery(id+"F0.wireOp",EDGE,"E2.2");var subQ2=makeQuery(id+"F0.imprint","INTERSECT",VERTEX,{"derivedFrom":[subQ1,subQ0]});Q75=makeQuery(id+"F0.imprint","IMPRINT",FACE,{"disambiguationData":[TD([[makeQuery(id+"F0.imprint","IMPRINT",EDGE,{"disambiguationData":[TD([[subQ2,1.0]])],"derivedFrom":subQ1}),-1.0]])]});}
            var Q76;
            {var subQ0=sQuery(id+"F0.wireOp",EDGE,"E8.1");var subQ1=sQuery(id+"F0.wireOp",EDGE,"E2.2");var subQ2=makeQuery(id+"F0.imprint","INTERSECT",VERTEX,{"derivedFrom":[subQ1,subQ0]});Q76=makeQuery(id+"F0.imprint","IMPRINT",FACE,{"disambiguationData":[TD([[makeQuery(id+"F0.imprint","IMPRINT",EDGE,{"disambiguationData":[TD([[subQ2,-1.0]])],"derivedFrom":subQ1}),1.0]])]});}
            var Q77;
            {var subQ0=sQuery(id+"F0.wireOp",EDGE,"E8.1");var subQ1=sQuery(id+"F0.wireOp",EDGE,"E2.2");var subQ2=makeQuery(id+"F0.imprint","INTERSECT",VERTEX,{"derivedFrom":[subQ1,subQ0]});Q77=makeQuery(id+"F0.imprint","IMPRINT",FACE,{"disambiguationData":[TD([[makeQuery(id+"F0.imprint","IMPRINT",EDGE,{"disambiguationData":[TD([[subQ2,-1.0]])],"derivedFrom":subQ1}),-1.0]])]});}
            var Q78;
            {var subQ0=sQuery(id+"F0.wireOp",EDGE,"E4.1");var subQ1=makeQuery(id+"F0.imprint","INTERSECT",VERTEX,{"derivedFrom":[sQuery(id+"F0.wireOp",EDGE,"E0"),subQ0]});Q78=makeQuery(id+"F0.imprint","IMPRINT",FACE,{"disambiguationData":[TD([[makeQuery(id+"F0.imprint","IMPRINT",EDGE,{"disambiguationData":[TD([[subQ1,1.0]])],"derivedFrom":subQ0}),1.0]])]});}
            var Q79;
            {var subQ0=sQuery(id+"F0.wireOp",EDGE,"E4.0");var subQ1=sQuery(id+"F0.wireOp",EDGE,"E2.2");var subQ2=makeQuery(id+"F0.imprint","INTERSECT",VERTEX,{"derivedFrom":[subQ1,subQ0]});Q79=makeQuery(id+"F0.imprint","IMPRINT",FACE,{"disambiguationData":[TD([[makeQuery(id+"F0.imprint","IMPRINT",EDGE,{"disambiguationData":[TD([[subQ2,-1.0]])],"derivedFrom":subQ1}),1.0]])]});}
            var Q80;
            {var subQ0=sQuery(id+"F0.wireOp",EDGE,"E2.2");var subQ1=makeQuery(id+"F0.imprint","INTERSECT",VERTEX,{"derivedFrom":[sQuery(id+"F0.wireOp",EDGE,"E0"),subQ0]});Q80=makeQuery(id+"F0.imprint","IMPRINT",FACE,{"disambiguationData":[TD([[makeQuery(id+"F0.imprint","IMPRINT",EDGE,{"disambiguationData":[TD([[subQ1,1.0]])],"derivedFrom":subQ0}),1.0]])]});}
            var Q81;
            {var subQ0=sQuery(id+"F0.wireOp",EDGE,"E4.1");var subQ1=sQuery(id+"F0.wireOp",EDGE,"E2.3");var subQ2=makeQuery(id+"F0.imprint","INTERSECT",VERTEX,{"derivedFrom":[subQ1,subQ0]});Q81=makeQuery(id+"F0.imprint","IMPRINT",FACE,{"disambiguationData":[TD([[makeQuery(id+"F0.imprint","IMPRINT",EDGE,{"disambiguationData":[TD([[subQ2,-1.0]])],"derivedFrom":subQ1}),-1.0]])]});}
            var Q82;
            {var subQ0=sQuery(id+"F0.wireOp",EDGE,"E2.3");var subQ1=makeQuery(id+"F0.imprint","INTERSECT",VERTEX,{"derivedFrom":[sQuery(id+"F0.wireOp",EDGE,"E0"),subQ0]});Q82=makeQuery(id+"F0.imprint","IMPRINT",FACE,{"disambiguationData":[TD([[makeQuery(id+"F0.imprint","IMPRINT",EDGE,{"disambiguationData":[TD([[subQ1,1.0]])],"derivedFrom":subQ0}),1.0]])]});}
            var Q83;
            {var subQ0=sQuery(id+"F0.wireOp",EDGE,"E6.2");var subQ1=sQuery(id+"F0.wireOp",EDGE,"E0");var subQ2=makeQuery(id+"F0.imprint","INTERSECT",VERTEX,{"derivedFrom":[subQ1,subQ0]});Q83=makeQuery(id+"F0.imprint","IMPRINT",FACE,{"disambiguationData":[TD([[makeQuery(id+"F0.imprint","IMPRINT",EDGE,{"disambiguationData":[TD([[subQ2,-1.0]])],"derivedFrom":subQ1}),-1.0]])]});}
            var Q84;
            {var subQ0=sQuery(id+"F0.wireOp",EDGE,"E8.1");var subQ1=sQuery(id+"F0.wireOp",EDGE,"E0");var subQ2=makeQuery(id+"F0.imprint","INTERSECT",VERTEX,{"derivedFrom":[subQ1,subQ0]});Q84=makeQuery(id+"F0.imprint","IMPRINT",FACE,{"disambiguationData":[TD([[makeQuery(id+"F0.imprint","IMPRINT",EDGE,{"disambiguationData":[TD([[subQ2,-1.0]])],"derivedFrom":subQ1}),-1.0]])]});}
            var Q85;
            {var subQ0=sQuery(id+"F0.wireOp",EDGE,"E2.2");var subQ1=sQuery(id+"F0.wireOp",EDGE,"E0");var subQ2=makeQuery(id+"F0.imprint","INTERSECT",VERTEX,{"derivedFrom":[subQ1,subQ0]});Q85=makeQuery(id+"F0.imprint","IMPRINT",FACE,{"disambiguationData":[TD([[makeQuery(id+"F0.imprint","IMPRINT",EDGE,{"disambiguationData":[TD([[subQ2,-1.0]])],"derivedFrom":subQ1}),-1.0]])]});}
            var Q86;
            {var subQ0=sQuery(id+"F0.wireOp",EDGE,"E2.3");var subQ1=sQuery(id+"F0.wireOp",EDGE,"E0");var subQ2=makeQuery(id+"F0.imprint","INTERSECT",VERTEX,{"derivedFrom":[subQ1,subQ0]});Q86=makeQuery(id+"F0.imprint","IMPRINT",FACE,{"disambiguationData":[TD([[makeQuery(id+"F0.imprint","IMPRINT",EDGE,{"disambiguationData":[TD([[subQ2,-1.0]])],"derivedFrom":subQ1}),-1.0]])]});}
            var Q87;
            {var subQ0=sQuery(id+"F0.wireOp",EDGE,"E0");var subQ4=makeQuery(id+"F0.imprint","INTERSECT",VERTEX,{"derivedFrom":[subQ0,sQuery(id+"F0.wireOp",EDGE,"E12.3.0")]});Q87=makeQuery(id+"F0.imprint","IMPRINT",FACE,{"disambiguationData":[TD([[makeQuery(id+"F0.imprint","IMPRINT",EDGE,{"disambiguationData":[TD([[subQ4,1.0]])],"derivedFrom":subQ0}),-1.0]])]});}
            var Q88;
            {var subQ0=sQuery(id+"F0.wireOp",EDGE,"E6.1");var subQ1=sQuery(id+"F0.wireOp",EDGE,"E2.1");var subQ2=makeQuery(id+"F0.imprint","INTERSECT",VERTEX,{"derivedFrom":[subQ1,subQ0]});Q88=makeQuery(id+"F0.imprint","IMPRINT",FACE,{"disambiguationData":[TD([[makeQuery(id+"F0.imprint","IMPRINT",EDGE,{"disambiguationData":[TD([[subQ2,1.0]])],"derivedFrom":subQ1}),-1.0]])]});}
            var Q89;
            {var subQ0=sQuery(id+"F0.wireOp",EDGE,"E8.5");var subQ1=sQuery(id+"F0.wireOp",EDGE,"E2.1");var subQ2=makeQuery(id+"F0.imprint","INTERSECT",VERTEX,{"derivedFrom":[subQ1,subQ0]});Q89=makeQuery(id+"F0.imprint","IMPRINT",FACE,{"disambiguationData":[TD([[makeQuery(id+"F0.imprint","IMPRINT",EDGE,{"disambiguationData":[TD([[subQ2,-1.0]])],"derivedFrom":subQ1}),1.0]])]});}
            var Q90;
            {var subQ0=sQuery(id+"F0.wireOp",EDGE,"E6.1");var subQ1=sQuery(id+"F0.wireOp",EDGE,"E2.1");var subQ2=makeQuery(id+"F0.imprint","INTERSECT",VERTEX,{"derivedFrom":[subQ1,subQ0]});Q90=makeQuery(id+"F0.imprint","IMPRINT",FACE,{"disambiguationData":[TD([[makeQuery(id+"F0.imprint","IMPRINT",EDGE,{"disambiguationData":[TD([[subQ2,1.0]])],"derivedFrom":subQ1}),1.0]])]});}
            var Q91;
            {var subQ0=sQuery(id+"F0.wireOp",EDGE,"E8.0");var subQ1=sQuery(id+"F0.wireOp",EDGE,"E2.2");var subQ2=makeQuery(id+"F0.imprint","INTERSECT",VERTEX,{"derivedFrom":[subQ1,subQ0]});Q91=makeQuery(id+"F0.imprint","IMPRINT",FACE,{"disambiguationData":[TD([[makeQuery(id+"F0.imprint","IMPRINT",EDGE,{"disambiguationData":[TD([[subQ2,-1.0]])],"derivedFrom":subQ1}),1.0]])]});}
            var Q92;
            {var subQ0=sQuery(id+"F0.wireOp",EDGE,"E4.5");var subQ1=sQuery(id+"F0.wireOp",EDGE,"E2.1");var subQ2=makeQuery(id+"F0.imprint","INTERSECT",VERTEX,{"derivedFrom":[subQ1,subQ0]});Q92=makeQuery(id+"F0.imprint","IMPRINT",FACE,{"disambiguationData":[TD([[makeQuery(id+"F0.imprint","IMPRINT",EDGE,{"disambiguationData":[TD([[subQ2,-1.0]])],"derivedFrom":subQ1}),1.0]])]});}
            var Q93;
            {var subQ0=sQuery(id+"F0.wireOp",EDGE,"E4.5");var subQ1=sQuery(id+"F0.wireOp",EDGE,"E4.0");var subQ2=makeQuery(id+"F0.imprint","INTERSECT",VERTEX,{"derivedFrom":[subQ1,subQ0]});Q93=makeQuery(id+"F0.imprint","IMPRINT",FACE,{"disambiguationData":[TD([[makeQuery(id+"F0.imprint","IMPRINT",EDGE,{"disambiguationData":[TD([[subQ2,-1.0]])],"derivedFrom":subQ1}),-1.0]])]});}
            var Q94;
            {var subQ0=sQuery(id+"F0.wireOp",EDGE,"E8.0");var subQ1=sQuery(id+"F0.wireOp",EDGE,"E2.2");var subQ2=makeQuery(id+"F0.imprint","INTERSECT",VERTEX,{"derivedFrom":[subQ1,subQ0]});Q94=makeQuery(id+"F0.imprint","IMPRINT",FACE,{"disambiguationData":[TD([[makeQuery(id+"F0.imprint","IMPRINT",EDGE,{"disambiguationData":[TD([[subQ2,-1.0]])],"derivedFrom":subQ1}),-1.0]])]});}
            var Q95;
            {var subQ0=sQuery(id+"F0.wireOp",EDGE,"E2.1");var subQ1=makeQuery(id+"F0.imprint","INTERSECT",VERTEX,{"derivedFrom":[sQuery(id+"F0.wireOp",EDGE,"E0"),subQ0]});Q95=makeQuery(id+"F0.imprint","IMPRINT",FACE,{"disambiguationData":[TD([[makeQuery(id+"F0.imprint","IMPRINT",EDGE,{"disambiguationData":[TD([[subQ1,1.0]])],"derivedFrom":subQ0}),1.0]])]});}
            var Q96;
            {var subQ0=sQuery(id+"F0.wireOp",EDGE,"E8.0");var subQ1=sQuery(id+"F0.wireOp",EDGE,"E2.1");var subQ2=makeQuery(id+"F0.imprint","INTERSECT",VERTEX,{"derivedFrom":[subQ1,subQ0]});Q96=makeQuery(id+"F0.imprint","IMPRINT",FACE,{"disambiguationData":[TD([[makeQuery(id+"F0.imprint","IMPRINT",EDGE,{"disambiguationData":[TD([[subQ2,-1.0]])],"derivedFrom":subQ1}),1.0]])]});}
            var Q97;
            {var subQ0=sQuery(id+"F0.wireOp",EDGE,"E4.0");var subQ1=makeQuery(id+"F0.imprint","INTERSECT",VERTEX,{"derivedFrom":[sQuery(id+"F0.wireOp",EDGE,"E0"),subQ0]});Q97=makeQuery(id+"F0.imprint","IMPRINT",FACE,{"disambiguationData":[TD([[makeQuery(id+"F0.imprint","IMPRINT",EDGE,{"disambiguationData":[TD([[subQ1,1.0]])],"derivedFrom":subQ0}),1.0]])]});}
            var Q98;
            {var subQ0=sQuery(id+"F0.wireOp",EDGE,"E8.5");var subQ1=sQuery(id+"F0.wireOp",EDGE,"E2.1");var subQ2=makeQuery(id+"F0.imprint","INTERSECT",VERTEX,{"derivedFrom":[subQ1,subQ0]});Q98=makeQuery(id+"F0.imprint","IMPRINT",FACE,{"disambiguationData":[TD([[makeQuery(id+"F0.imprint","IMPRINT",EDGE,{"disambiguationData":[TD([[subQ2,-1.0]])],"derivedFrom":subQ1}),-1.0]])]});}
            var Q99;
            {var subQ0=sQuery(id+"F0.wireOp",EDGE,"E4.0");var subQ1=sQuery(id+"F0.wireOp",EDGE,"E2.2");var subQ2=makeQuery(id+"F0.imprint","INTERSECT",VERTEX,{"derivedFrom":[subQ1,subQ0]});Q99=makeQuery(id+"F0.imprint","IMPRINT",FACE,{"disambiguationData":[TD([[makeQuery(id+"F0.imprint","IMPRINT",EDGE,{"disambiguationData":[TD([[subQ2,-1.0]])],"derivedFrom":subQ1}),-1.0]])]});}
            var Q100;
            {var subQ0=sQuery(id+"F0.wireOp",EDGE,"E2.2");var subQ1=sQuery(id+"F0.wireOp",EDGE,"E2.1");var subQ2=makeQuery(id+"F0.imprint","INTERSECT",VERTEX,{"derivedFrom":[subQ1,subQ0]});Q100=makeQuery(id+"F0.imprint","IMPRINT",FACE,{"disambiguationData":[TD([[makeQuery(id+"F0.imprint","IMPRINT",EDGE,{"disambiguationData":[TD([[subQ2,1.0]])],"derivedFrom":subQ1}),-1.0]])]});}
            var Q101;
            {var subQ0=sQuery(id+"F0.wireOp",EDGE,"E0");var subQ1=makeQuery(id+"F0.imprint","INTERSECT",VERTEX,{"derivedFrom":[subQ0,sQuery(id+"F0.wireOp",EDGE,"E12.4.1")]});Q101=makeQuery(id+"F0.imprint","IMPRINT",FACE,{"disambiguationData":[TD([[makeQuery(id+"F0.imprint","IMPRINT",EDGE,{"disambiguationData":[TD([[subQ1,1.0]])],"derivedFrom":subQ0}),-1.0]])]});}
            var Q102;
            {var subQ0=sQuery(id+"F0.wireOp",EDGE,"E4.5");var subQ1=sQuery(id+"F0.wireOp",EDGE,"E2.1");var subQ2=makeQuery(id+"F0.imprint","INTERSECT",VERTEX,{"derivedFrom":[subQ1,subQ0]});Q102=makeQuery(id+"F0.imprint","IMPRINT",FACE,{"disambiguationData":[TD([[makeQuery(id+"F0.imprint","IMPRINT",EDGE,{"disambiguationData":[TD([[subQ2,-1.0]])],"derivedFrom":subQ1}),-1.0]])]});}
            var Q103;
            {var subQ0=sQuery(id+"F0.wireOp",EDGE,"E8.0");var subQ1=sQuery(id+"F0.wireOp",EDGE,"E2.1");var subQ2=makeQuery(id+"F0.imprint","INTERSECT",VERTEX,{"derivedFrom":[subQ1,subQ0]});Q103=makeQuery(id+"F0.imprint","IMPRINT",FACE,{"disambiguationData":[TD([[makeQuery(id+"F0.imprint","IMPRINT",EDGE,{"disambiguationData":[TD([[subQ2,-1.0]])],"derivedFrom":subQ1}),-1.0]])]});}
            var Q104;
            {var subQ0=sQuery(id+"F0.wireOp",EDGE,"E6.0");var subQ1=sQuery(id+"F0.wireOp",EDGE,"E0");var subQ2=makeQuery(id+"F0.imprint","INTERSECT",VERTEX,{"derivedFrom":[subQ1,subQ0]});Q104=makeQuery(id+"F0.imprint","IMPRINT",FACE,{"disambiguationData":[TD([[makeQuery(id+"F0.imprint","IMPRINT",EDGE,{"disambiguationData":[TD([[subQ2,-1.0]])],"derivedFrom":subQ1}),-1.0]])]});}
            var Q105;
            {var subQ0=sQuery(id+"F0.wireOp",EDGE,"E2.1");var subQ1=sQuery(id+"F0.wireOp",EDGE,"E0");var subQ2=makeQuery(id+"F0.imprint","INTERSECT",VERTEX,{"derivedFrom":[subQ1,subQ0]});Q105=makeQuery(id+"F0.imprint","IMPRINT",FACE,{"disambiguationData":[TD([[makeQuery(id+"F0.imprint","IMPRINT",EDGE,{"disambiguationData":[TD([[subQ2,-1.0]])],"derivedFrom":subQ1}),-1.0]])]});}
            var Q106;
            {var subQ0=sQuery(id+"F0.wireOp",EDGE,"E4.0");var subQ1=sQuery(id+"F0.wireOp",EDGE,"E0");var subQ2=makeQuery(id+"F0.imprint","INTERSECT",VERTEX,{"derivedFrom":[subQ1,subQ0]});Q106=makeQuery(id+"F0.imprint","IMPRINT",FACE,{"disambiguationData":[TD([[makeQuery(id+"F0.imprint","IMPRINT",EDGE,{"disambiguationData":[TD([[subQ2,1.0]])],"derivedFrom":subQ1}),-1.0]])]});}
            var Q107;
            {var subQ0=sQuery(id+"F0.wireOp",EDGE,"E0");var subQ1=makeQuery(id+"F0.imprint","INTERSECT",VERTEX,{"derivedFrom":[subQ0,sQuery(id+"F0.wireOp",EDGE,"E12.4.0")]});Q107=makeQuery(id+"F0.imprint","IMPRINT",FACE,{"disambiguationData":[TD([[makeQuery(id+"F0.imprint","IMPRINT",EDGE,{"disambiguationData":[TD([[subQ1,1.0]])],"derivedFrom":subQ0}),-1.0]])]});}
            var Q108;
            {var subQ0=sQuery(id+"F0.wireOp",EDGE,"E8.5");var subQ1=sQuery(id+"F0.wireOp",EDGE,"E2.0");var subQ2=makeQuery(id+"F0.imprint","INTERSECT",VERTEX,{"derivedFrom":[subQ1,subQ0]});Q108=makeQuery(id+"F0.imprint","IMPRINT",FACE,{"disambiguationData":[TD([[makeQuery(id+"F0.imprint","IMPRINT",EDGE,{"disambiguationData":[TD([[subQ2,-1.0]])],"derivedFrom":subQ1}),-1.0]])]});}
            var Q109;
            {var subQ0=sQuery(id+"F0.wireOp",EDGE,"E4.4");var subQ1=sQuery(id+"F0.wireOp",EDGE,"E2.0");var subQ2=makeQuery(id+"F0.imprint","INTERSECT",VERTEX,{"derivedFrom":[subQ1,subQ0]});Q109=makeQuery(id+"F0.imprint","IMPRINT",FACE,{"disambiguationData":[TD([[makeQuery(id+"F0.imprint","IMPRINT",EDGE,{"disambiguationData":[TD([[subQ2,-1.0]])],"derivedFrom":subQ1}),-1.0]])]});}
            var Q110;
            {var subQ0=sQuery(id+"F0.wireOp",EDGE,"E0");var subQ1=makeQuery(id+"F0.imprint","INTERSECT",VERTEX,{"derivedFrom":[subQ0,sQuery(id+"F0.wireOp",EDGE,"E10")]});Q110=makeQuery(id+"F0.imprint","IMPRINT",FACE,{"disambiguationData":[TD([[makeQuery(id+"F0.imprint","IMPRINT",EDGE,{"disambiguationData":[TD([[subQ1,1.0]])],"derivedFrom":subQ0}),-1.0]])]});}
            var Q111;
            {var subQ0=sQuery(id+"F0.wireOp",EDGE,"E8.4");var subQ1=sQuery(id+"F0.wireOp",EDGE,"E2.0");var subQ2=makeQuery(id+"F0.imprint","INTERSECT",VERTEX,{"derivedFrom":[subQ1,subQ0]});Q111=makeQuery(id+"F0.imprint","IMPRINT",FACE,{"disambiguationData":[TD([[makeQuery(id+"F0.imprint","IMPRINT",EDGE,{"disambiguationData":[TD([[subQ2,-1.0]])],"derivedFrom":subQ1}),1.0]])]});}
            var Q112;
            {var subQ0=sQuery(id+"F0.wireOp",EDGE,"E4.5");var subQ1=makeQuery(id+"F0.imprint","INTERSECT",VERTEX,{"derivedFrom":[sQuery(id+"F0.wireOp",EDGE,"E0"),subQ0]});Q112=makeQuery(id+"F0.imprint","IMPRINT",FACE,{"disambiguationData":[TD([[makeQuery(id+"F0.imprint","IMPRINT",EDGE,{"disambiguationData":[TD([[subQ1,1.0]])],"derivedFrom":subQ0}),1.0]])]});}
            var Q113;
            {var subQ0=sQuery(id+"F0.wireOp",EDGE,"E6.0");var subQ1=sQuery(id+"F0.wireOp",EDGE,"E2.0");var subQ2=makeQuery(id+"F0.imprint","INTERSECT",VERTEX,{"derivedFrom":[subQ1,subQ0]});Q113=makeQuery(id+"F0.imprint","IMPRINT",FACE,{"disambiguationData":[TD([[makeQuery(id+"F0.imprint","IMPRINT",EDGE,{"disambiguationData":[TD([[subQ2,1.0]])],"derivedFrom":subQ1}),1.0]])]});}
            var Q114;
            {var subQ0=sQuery(id+"F0.wireOp",EDGE,"E2.1");var subQ1=sQuery(id+"F0.wireOp",EDGE,"E2.0");var subQ2=makeQuery(id+"F0.imprint","INTERSECT",VERTEX,{"derivedFrom":[subQ1,subQ0]});Q114=makeQuery(id+"F0.imprint","IMPRINT",FACE,{"disambiguationData":[TD([[makeQuery(id+"F0.imprint","IMPRINT",EDGE,{"disambiguationData":[TD([[subQ2,1.0]])],"derivedFrom":subQ1}),-1.0]])]});}
            var Q115;
            {var subQ0=sQuery(id+"F0.wireOp",EDGE,"E6.0");var subQ1=sQuery(id+"F0.wireOp",EDGE,"E2.0");var subQ2=makeQuery(id+"F0.imprint","INTERSECT",VERTEX,{"derivedFrom":[subQ1,subQ0]});Q115=makeQuery(id+"F0.imprint","IMPRINT",FACE,{"disambiguationData":[TD([[makeQuery(id+"F0.imprint","IMPRINT",EDGE,{"disambiguationData":[TD([[subQ2,1.0]])],"derivedFrom":subQ1}),-1.0]])]});}
            var Q116;
            {var subQ0=sQuery(id+"F0.wireOp",EDGE,"E4.5");var subQ1=sQuery(id+"F0.wireOp",EDGE,"E4.4");var subQ2=makeQuery(id+"F0.imprint","INTERSECT",VERTEX,{"derivedFrom":[subQ1,subQ0]});Q116=makeQuery(id+"F0.imprint","IMPRINT",FACE,{"disambiguationData":[TD([[makeQuery(id+"F0.imprint","IMPRINT",EDGE,{"disambiguationData":[TD([[subQ2,1.0]])],"derivedFrom":subQ1}),-1.0]])]});}
            var Q117;
            {var subQ0=sQuery(id+"F0.wireOp",EDGE,"E8.5");var subQ1=sQuery(id+"F0.wireOp",EDGE,"E2.0");var subQ2=makeQuery(id+"F0.imprint","INTERSECT",VERTEX,{"derivedFrom":[subQ1,subQ0]});Q117=makeQuery(id+"F0.imprint","IMPRINT",FACE,{"disambiguationData":[TD([[makeQuery(id+"F0.imprint","IMPRINT",EDGE,{"disambiguationData":[TD([[subQ2,-1.0]])],"derivedFrom":subQ1}),1.0]])]});}
            var Q118;
            {var subQ0=sQuery(id+"F0.wireOp",EDGE,"E4.4");var subQ1=sQuery(id+"F0.wireOp",EDGE,"E2.0");var subQ2=makeQuery(id+"F0.imprint","INTERSECT",VERTEX,{"derivedFrom":[subQ1,subQ0]});Q118=makeQuery(id+"F0.imprint","IMPRINT",FACE,{"disambiguationData":[TD([[makeQuery(id+"F0.imprint","IMPRINT",EDGE,{"disambiguationData":[TD([[subQ2,-1.0]])],"derivedFrom":subQ1}),1.0]])]});}
            var Q119;
            {var subQ0=sQuery(id+"F0.wireOp",EDGE,"E4.5");var subQ1=sQuery(id+"F0.wireOp",EDGE,"E0");var subQ2=makeQuery(id+"F0.imprint","INTERSECT",VERTEX,{"derivedFrom":[subQ1,subQ0]});Q119=makeQuery(id+"F0.imprint","IMPRINT",FACE,{"disambiguationData":[TD([[makeQuery(id+"F0.imprint","IMPRINT",EDGE,{"disambiguationData":[TD([[subQ2,-1.0]])],"derivedFrom":subQ1}),-1.0]])]});}
            var Q120;
            {var subQ0=sQuery(id+"F0.wireOp",EDGE,"E2.0");var subQ1=makeQuery(id+"F0.imprint","INTERSECT",VERTEX,{"derivedFrom":[sQuery(id+"F0.wireOp",EDGE,"E0"),subQ0]});Q120=makeQuery(id+"F0.imprint","IMPRINT",FACE,{"disambiguationData":[TD([[makeQuery(id+"F0.imprint","IMPRINT",EDGE,{"disambiguationData":[TD([[subQ1,1.0]])],"derivedFrom":subQ0}),1.0]])]});}
            var Q121;
            {var subQ0=sQuery(id+"F0.wireOp",EDGE,"E0");var subQ1=makeQuery(id+"F0.imprint","INTERSECT",VERTEX,{"derivedFrom":[subQ0,sQuery(id+"F0.wireOp",EDGE,"E11")]});Q121=makeQuery(id+"F0.imprint","IMPRINT",FACE,{"disambiguationData":[TD([[makeQuery(id+"F0.imprint","IMPRINT",EDGE,{"disambiguationData":[TD([[subQ1,1.0]])],"derivedFrom":subQ0}),-1.0]])]});}
            extrude(context, id + "F1", {"entities" : qUnion([Q0, Q1, Q2, Q3, Q4, Q5, Q6, Q7, Q8, Q9, Q10, Q11, Q12, Q13, Q14, Q15, Q16, Q17, Q18, Q19, Q20, Q21, Q22, Q23, Q24, Q25, Q26, Q27, Q28, Q29, Q30, Q31, Q32, Q33, Q34, Q35, Q36, Q37, Q38, Q39, Q40, Q41, Q42, Q43, Q44, Q45, Q46, Q47, Q48, Q49, Q50, Q51, Q52, Q53, Q54, Q55, Q56, Q57, Q58, Q59, Q60, Q61, Q62, Q63, Q64, Q65, Q66, Q67, Q68, Q69, Q70, Q71, Q72, Q73, Q74, Q75, Q76, Q77, Q78, Q79, Q80, Q81, Q82, Q83, Q84, Q85, Q86, Q87, Q88, Q89, Q90, Q91, Q92, Q93, Q94, Q95, Q96, Q97, Q98, Q99, Q100, Q101, Q102, Q103, Q104, Q105, Q106, Q107, Q108, Q109, Q110, Q111, Q112, Q113, Q114, Q115, Q116, Q117, Q118, Q119, Q120, Q121]), "depth" : 10 * mm, "offsetDistance" : 25 * mm});
        }
        {
            var Q0;
            Q0=makeQuery(id+"F1.opExtrude","CAP_FACE",FACE,{"disambiguationData":[OSD([sQuery(id+"F0.wireOp",EDGE,"E0"),sQuery(id+"F0.wireOp",EDGE,"E2.0"),sQuery(id+"F0.wireOp",EDGE,"E2.1"),sQuery(id+"F0.wireOp",EDGE,"E2.2"),sQuery(id+"F0.wireOp",EDGE,"E2.3"),sQuery(id+"F0.wireOp",EDGE,"E2.4"),sQuery(id+"F0.wireOp",EDGE,"E2.5"),sQuery(id+"F0.wireOp",EDGE,"E4.0"),sQuery(id+"F0.wireOp",EDGE,"E4.1"),sQuery(id+"F0.wireOp",EDGE,"E4.2"),sQuery(id+"F0.wireOp",EDGE,"E4.3"),sQuery(id+"F0.wireOp",EDGE,"E4.4"),sQuery(id+"F0.wireOp",EDGE,"E4.5"),sQuery(id+"F0.wireOp",EDGE,"E6.0"),sQuery(id+"F0.wireOp",EDGE,"E6.1"),sQuery(id+"F0.wireOp",EDGE,"E6.2"),sQuery(id+"F0.wireOp",EDGE,"E6.3"),sQuery(id+"F0.wireOp",EDGE,"E6.4"),sQuery(id+"F0.wireOp",EDGE,"E6.5"),sQuery(id+"F0.wireOp",EDGE,"E8.0"),sQuery(id+"F0.wireOp",EDGE,"E8.1"),sQuery(id+"F0.wireOp",EDGE,"E8.2"),sQuery(id+"F0.wireOp",EDGE,"E8.3"),sQuery(id+"F0.wireOp",EDGE,"E8.4"),sQuery(id+"F0.wireOp",EDGE,"E8.5"),sQuery(id+"F0.wireOp",EDGE,"E10"),sQuery(id+"F0.wireOp",EDGE,"E11"),sQuery(id+"F0.wireOp",EDGE,"E12.1.0"),sQuery(id+"F0.wireOp",EDGE,"E12.1.1"),sQuery(id+"F0.wireOp",EDGE,"E12.2.0"),sQuery(id+"F0.wireOp",EDGE,"E12.2.1"),sQuery(id+"F0.wireOp",EDGE,"E12.3.0"),sQuery(id+"F0.wireOp",EDGE,"E12.3.1"),sQuery(id+"F0.wireOp",EDGE,"E12.4.0"),sQuery(id+"F0.wireOp",EDGE,"E12.4.1"),sQuery(id+"F0.wireOp",EDGE,"E13"),sQuery(id+"F0.wireOp",EDGE,"E14")])],"isStart":false});
            var sketch = newSketch(context, id + "F2", { "sketchPlane" : qUnion([Q0])});
            skCircle(sketch, "E15", {"center": v(0, 0) * mm, "radius": 5 * mm});
            skSolve(sketch);
        }
        {
            var Q0;
            Q0=makeQuery(id+"F2.imprint","IMPRINT",FACE,{"disambiguationData":[TD([[makeQuery(id+"F2.imprint","IMPRINT",EDGE,{"derivedFrom":sQuery(id+"F2.wireOp",EDGE,"E15")}),1.0]])]});
            extrude(context, id + "F3", {"entities" : qUnion([Q0]), "operationType" : NewBodyOperationType.ADD, "depth" : 2 * mm, "offsetDistance" : 25 * mm});
        }
        {
            var Q0;
            Q0=makeQuery(id+"F3.opExtrude","CAP_FACE",FACE,{"disambiguationData":[OSD([sQuery(id+"F0.wireOp",EDGE,"E14"),sQuery(id+"F2.wireOp",EDGE,"E15")])],"isStart":false});
            var sketch = newSketch(context, id + "F4", { "sketchPlane" : qUnion([Q0])});
            skCircle(sketch, "E16", {"center": v(0, 0) * mm, "radius": 2.4 * mm});
            skSolve(sketch);
        }
        {
            var Q0;
            Q0 = qSketchRegion(id + "F4", true);
            extrude(context, id + "F5", {"entities" : qUnion([Q0]), "operationType" : NewBodyOperationType.REMOVE, "oppositeDirection" : true, "depth" : 3 * mm, "offsetDistance" : 25 * mm});
        }
        {
            var Q0;
            Q0=makeQuery(id+"F1.opExtrude","CAP_FACE",FACE,{"disambiguationData":[OSD([sQuery(id+"F0.wireOp",EDGE,"E0"),sQuery(id+"F0.wireOp",EDGE,"E2.0"),sQuery(id+"F0.wireOp",EDGE,"E2.1"),sQuery(id+"F0.wireOp",EDGE,"E2.2"),sQuery(id+"F0.wireOp",EDGE,"E2.3"),sQuery(id+"F0.wireOp",EDGE,"E2.4"),sQuery(id+"F0.wireOp",EDGE,"E2.5"),sQuery(id+"F0.wireOp",EDGE,"E4.0"),sQuery(id+"F0.wireOp",EDGE,"E4.1"),sQuery(id+"F0.wireOp",EDGE,"E4.2"),sQuery(id+"F0.wireOp",EDGE,"E4.3"),sQuery(id+"F0.wireOp",EDGE,"E4.4"),sQuery(id+"F0.wireOp",EDGE,"E4.5"),sQuery(id+"F0.wireOp",EDGE,"E6.0"),sQuery(id+"F0.wireOp",EDGE,"E6.1"),sQuery(id+"F0.wireOp",EDGE,"E6.2"),sQuery(id+"F0.wireOp",EDGE,"E6.3"),sQuery(id+"F0.wireOp",EDGE,"E6.4"),sQuery(id+"F0.wireOp",EDGE,"E6.5"),sQuery(id+"F0.wireOp",EDGE,"E8.0"),sQuery(id+"F0.wireOp",EDGE,"E8.1"),sQuery(id+"F0.wireOp",EDGE,"E8.2"),sQuery(id+"F0.wireOp",EDGE,"E8.3"),sQuery(id+"F0.wireOp",EDGE,"E8.4"),sQuery(id+"F0.wireOp",EDGE,"E8.5"),sQuery(id+"F0.wireOp",EDGE,"E10"),sQuery(id+"F0.wireOp",EDGE,"E11"),sQuery(id+"F0.wireOp",EDGE,"E12.1.0"),sQuery(id+"F0.wireOp",EDGE,"E12.1.1"),sQuery(id+"F0.wireOp",EDGE,"E12.2.0"),sQuery(id+"F0.wireOp",EDGE,"E12.2.1"),sQuery(id+"F0.wireOp",EDGE,"E12.3.0"),sQuery(id+"F0.wireOp",EDGE,"E12.3.1"),sQuery(id+"F0.wireOp",EDGE,"E12.4.0"),sQuery(id+"F0.wireOp",EDGE,"E12.4.1"),sQuery(id+"F0.wireOp",EDGE,"E13"),sQuery(id+"F0.wireOp",EDGE,"E14")])],"isStart":true});
            var sketch = newSketch(context, id + "F6", { "sketchPlane" : qUnion([Q0])});
            skCircle(sketch, "E17", {"center": v(0, 0) * mm, "radius": 5 * mm});
            skSolve(sketch);
        }
        {
            var Q0;
            Q0 = qSketchRegion(id + "F6", true);
            extrude(context, id + "F7", {"entities" : qUnion([Q0]), "operationType" : NewBodyOperationType.REMOVE, "oppositeDirection" : true, "depth" : 8 * mm, "offsetDistance" : 25 * mm});
        }
        {
            var Q0;
            Q0=makeQuery(id+"F1.opExtrude","SWEPT_EDGE",EDGE,{"disambiguationData":[OSD([sQuery(id+"F0.wireOp",EDGE,"E0"),sQuery(id+"F0.wireOp",EDGE,"E12.4.0")])]});
            var Q1;
            Q1=makeQuery(id+"F1.opExtrude","SWEPT_EDGE",EDGE,{"disambiguationData":[OSD([sQuery(id+"F0.wireOp",EDGE,"E12.4.0"),sQuery(id+"F0.wireOp",EDGE,"E13")])]});
            var Q2;
            Q2=makeQuery(id+"F1.opExtrude","SWEPT_EDGE",EDGE,{"disambiguationData":[OSD([sQuery(id+"F0.wireOp",EDGE,"E12.3.1"),sQuery(id+"F0.wireOp",EDGE,"E13")])]});
            var Q3;
            Q3=makeQuery(id+"F1.opExtrude","SWEPT_EDGE",EDGE,{"disambiguationData":[OSD([sQuery(id+"F0.wireOp",EDGE,"E0"),sQuery(id+"F0.wireOp",EDGE,"E12.3.1")])]});
            var Q4;
            Q4=makeQuery(id+"F1.opExtrude","SWEPT_EDGE",EDGE,{"disambiguationData":[OSD([sQuery(id+"F0.wireOp",EDGE,"E0"),sQuery(id+"F0.wireOp",EDGE,"E12.3.0")])]});
            var Q5;
            Q5=makeQuery(id+"F1.opExtrude","SWEPT_EDGE",EDGE,{"disambiguationData":[OSD([sQuery(id+"F0.wireOp",EDGE,"E12.2.0"),sQuery(id+"F0.wireOp",EDGE,"E13")])]});
            var Q6;
            Q6=makeQuery(id+"F1.opExtrude","SWEPT_EDGE",EDGE,{"disambiguationData":[OSD([sQuery(id+"F0.wireOp",EDGE,"E12.2.1"),sQuery(id+"F0.wireOp",EDGE,"E13")])]});
            var Q7;
            Q7=makeQuery(id+"F1.opExtrude","SWEPT_EDGE",EDGE,{"disambiguationData":[OSD([sQuery(id+"F0.wireOp",EDGE,"E12.3.0"),sQuery(id+"F0.wireOp",EDGE,"E13")])]});
            var Q8;
            Q8=makeQuery(id+"F1.opExtrude","SWEPT_EDGE",EDGE,{"disambiguationData":[OSD([sQuery(id+"F0.wireOp",EDGE,"E0"),sQuery(id+"F0.wireOp",EDGE,"E12.2.1")])]});
            var Q9;
            Q9=makeQuery(id+"F1.opExtrude","SWEPT_EDGE",EDGE,{"disambiguationData":[OSD([sQuery(id+"F0.wireOp",EDGE,"E0"),sQuery(id+"F0.wireOp",EDGE,"E12.2.0")])]});
            var Q10;
            Q10=makeQuery(id+"F1.opExtrude","SWEPT_EDGE",EDGE,{"disambiguationData":[OSD([sQuery(id+"F0.wireOp",EDGE,"E0"),sQuery(id+"F0.wireOp",EDGE,"E12.1.1")])]});
            var Q11;
            Q11=makeQuery(id+"F1.opExtrude","SWEPT_EDGE",EDGE,{"disambiguationData":[OSD([sQuery(id+"F0.wireOp",EDGE,"E0"),sQuery(id+"F0.wireOp",EDGE,"E12.1.0")])]});
            var Q12;
            Q12=makeQuery(id+"F1.opExtrude","SWEPT_EDGE",EDGE,{"disambiguationData":[OSD([sQuery(id+"F0.wireOp",EDGE,"E0"),sQuery(id+"F0.wireOp",EDGE,"E10")])]});
            var Q13;
            Q13=makeQuery(id+"F1.opExtrude","SWEPT_EDGE",EDGE,{"disambiguationData":[OSD([sQuery(id+"F0.wireOp",EDGE,"E0"),sQuery(id+"F0.wireOp",EDGE,"E11")])]});
            var Q14;
            Q14=makeQuery(id+"F1.opExtrude","SWEPT_EDGE",EDGE,{"disambiguationData":[OSD([sQuery(id+"F0.wireOp",EDGE,"E0"),sQuery(id+"F0.wireOp",EDGE,"E12.4.1")])]});
            var Q15;
            Q15=makeQuery(id+"F1.opExtrude","SWEPT_EDGE",EDGE,{"disambiguationData":[OSD([sQuery(id+"F0.wireOp",EDGE,"E12.4.1"),sQuery(id+"F0.wireOp",EDGE,"E13")])]});
            var Q16;
            Q16=makeQuery(id+"F1.opExtrude","SWEPT_EDGE",EDGE,{"disambiguationData":[OSD([sQuery(id+"F0.wireOp",EDGE,"E11"),sQuery(id+"F0.wireOp",EDGE,"E13")])]});
            var Q17;
            Q17=makeQuery(id+"F1.opExtrude","SWEPT_EDGE",EDGE,{"disambiguationData":[OSD([sQuery(id+"F0.wireOp",EDGE,"E10"),sQuery(id+"F0.wireOp",EDGE,"E13")])]});
            var Q18;
            Q18=makeQuery(id+"F1.opExtrude","SWEPT_EDGE",EDGE,{"disambiguationData":[OSD([sQuery(id+"F0.wireOp",EDGE,"E12.1.0"),sQuery(id+"F0.wireOp",EDGE,"E13")])]});
            var Q19;
            Q19=makeQuery(id+"F1.opExtrude","SWEPT_EDGE",EDGE,{"disambiguationData":[OSD([sQuery(id+"F0.wireOp",EDGE,"E12.1.1"),sQuery(id+"F0.wireOp",EDGE,"E13")])]});
            fillet(context, id + "F8", {"entities" : qUnion([Q0, Q1, Q2, Q3, Q4, Q5, Q6, Q7, Q8, Q9, Q10, Q11, Q12, Q13, Q14, Q15, Q16, Q17, Q18, Q19]), "radius" : 2.4 * mm, "tangentPropagation" : true, "allowEdgeOverflow" : false});
        }
    });
